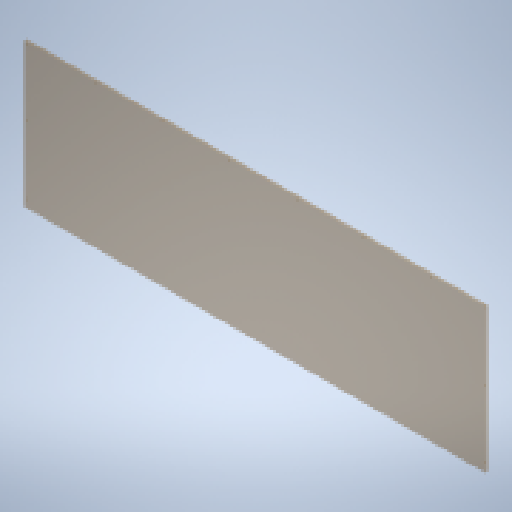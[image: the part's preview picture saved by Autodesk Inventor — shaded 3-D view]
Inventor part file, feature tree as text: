
AUTODESK INVENTOR PART (.ipt)
format: ipt  version: 2024 (Build 280153000, 153)  size: 273,408 bytes
history: native  units: in
note: dims shown in document units (in); Inventor stores cm internally (conversion verified against a paired STEP export)
features: pattern_linear x3, extrude x2, sketch x2
ambient origin geometry x8: Origin, YZ Plane, XZ Plane, XY Plane, X Axis, Y Axis, Z Axis, Center Point
bodies: Solid1 (feature_tree)
feature tree (7):
  extrude  "Extrusion1"  Depth=30.0in
  extrude  "Extrusion2"  Depth=0.5in
  pattern_linear  "Rectangular Pattern1"  Spacing1=0.5in  [1 undecoded]
  pattern_linear  "Rectangular Pattern2"  Spacing1=0.5in  [1 undecoded]
  pattern_linear  "Rectangular Pattern3"  Spacing1=0.0in  [1 undecoded]
  sketch  "Sketch1"  dims[d0=96.0in d1=30.0in]
  sketch  "Sketch2"  dims[d2=0.5in d3=0.0in d4=0.201in d5=0.5in d6=0.5in d7=0.0in d8=0.0in d9=1.1811in d11=14.0in d12=3.1496in d14=14.0in d15=0.7874in d17=95.0in]
note: 3 required parameter values undecoded (feature->parameter linkage not recoverable at this tier; creation-order binding heuristic only, values carry confidence <= 0.55)
